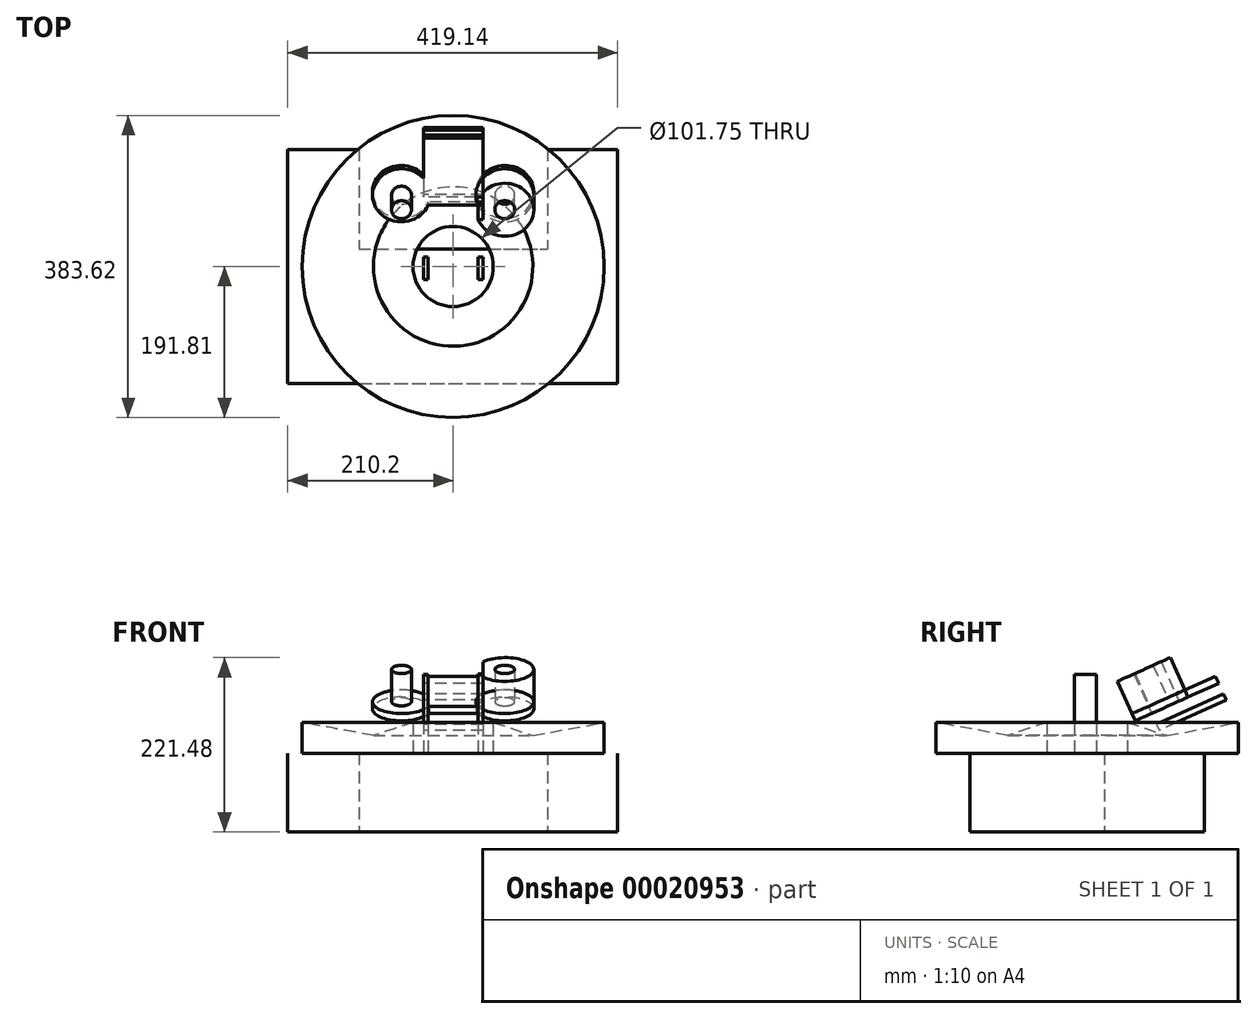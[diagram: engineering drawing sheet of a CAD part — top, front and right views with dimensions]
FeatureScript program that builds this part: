
annotation { "Feature Type Name" : "Feature", "Feature Type Description" : "" }
export const myFeature = defineFeature(function(context is Context, id is Id, definition is map)
    precondition{}
    {
        {
            var Q0;
            Q0=qCreatedBy(makeId("Top.planeOp"),FACE);
            var sketch = newSketch(context, id + "F0", { "sketchPlane" : qUnion([Q0])});
            skLineSegment(sketch, "E0.bottom", {"start": v(-210.2, 148.75) * mm, "end": v(208.94, 148.75) * mm});
            skLineSegment(sketch, "E0.top", {"start": v(-210.2, -148.75) * mm, "end": v(208.94, -148.75) * mm});
            skLineSegment(sketch, "E0.left", {"start": v(-210.2, 148.75) * mm, "end": v(-210.2, -148.75) * mm});
            skLineSegment(sketch, "E0.right", {"start": v(208.94, 148.75) * mm, "end": v(208.94, -148.75) * mm});
            skLineSegment(sketch, "E1", {"start": v(-0.63, 148.75) * mm, "end": v(0, 0) * mm, "construction": true});
            skLineSegment(sketch, "E2", {"start": v(0, 0) * mm, "end": v(0, -148.75) * mm, "construction": true});
            skLineSegment(sketch, "E3", {"start": v(0, 0) * mm, "end": v(-210.2, -0.9) * mm, "construction": true});
            skLineSegment(sketch, "E4", {"start": v(-210.2, -0.9) * mm, "end": v(0, 0) * mm, "construction": true});
            skLineSegment(sketch, "E5", {"start": v(0, 0) * mm, "end": v(208.94, 0.89) * mm, "construction": true});
            skLineSegment(sketch, "E6.bottom", {"start": v(-119.71, 148.75) * mm, "end": v(119.71, 148.75) * mm});
            skLineSegment(sketch, "E6.top", {"start": v(-119.71, 21.99) * mm, "end": v(119.71, 21.99) * mm});
            skLineSegment(sketch, "E6.left", {"start": v(-119.71, 148.75) * mm, "end": v(-119.71, 21.99) * mm});
            skLineSegment(sketch, "E6.right", {"start": v(119.71, 148.75) * mm, "end": v(119.71, 21.99) * mm});
            skPoint(sketch, "E7", {"position": v(0, 21.99) * mm});
            skSolve(sketch);
        }
        {
            var Q0;
            Q0=makeQuery(id+"F0.imprint","IMPRINT",FACE,{"disambiguationData":[TD([[makeQuery(id+"F0.imprint","IMPRINT",EDGE,{"derivedFrom":sQuery(id+"F0.wireOp",EDGE,"E0.top")}),1.0]])]});
            extrude(context, id + "F1", {"entities" : qUnion([Q0]), "depth" : 100 * mm});
        }
        {
            var Q0;
            Q0=makeQuery(id+"F1.opExtrude","CAP_FACE",FACE,{"disambiguationData":[OSD([sQuery(id+"F0.wireOp",EDGE,"E0.bottom"),sQuery(id+"F0.wireOp",EDGE,"E0.top"),sQuery(id+"F0.wireOp",EDGE,"E0.left"),sQuery(id+"F0.wireOp",EDGE,"E0.right"),sQuery(id+"F0.wireOp",EDGE,"E6.top"),sQuery(id+"F0.wireOp",EDGE,"E6.left"),sQuery(id+"F0.wireOp",EDGE,"E6.right")])],"isStart":false});
            var sketch = newSketch(context, id + "F2", { "sketchPlane" : qUnion([Q0])});
            skCircle(sketch, "E8", {"center": v(0, 0) * mm, "radius": 191.8 * mm});
            skCircle(sketch, "E9", {"center": v(0, 0) * mm, "radius": 50.88 * mm});
            skLineSegment(sketch, "E10.bottom", {"start": v(-37.83, 11.78) * mm, "end": v(-31.7, 11.78) * mm});
            skLineSegment(sketch, "E10.top", {"start": v(-37.83, -16.3) * mm, "end": v(-31.7, -16.3) * mm});
            skLineSegment(sketch, "E10.left", {"start": v(-37.83, 11.78) * mm, "end": v(-37.83, -16.3) * mm});
            skLineSegment(sketch, "E10.right", {"start": v(-31.7, 11.78) * mm, "end": v(-31.7, -16.3) * mm});
            skLineSegment(sketch, "E11", {"start": v(0, 0) * mm, "end": v(0, -33.08) * mm, "construction": true});
            skPoint(sketch, "E11.endSnap0", {"position": v(0, 21.99) * mm});
            skLineSegment(sketch, "E12.MirrorCS", {"start": v(37.83, 11.78) * mm, "end": v(37.83, -16.3) * mm});
            skLineSegment(sketch, "E13.MirrorCS", {"start": v(37.83, -16.3) * mm, "end": v(31.7, -16.3) * mm});
            skLineSegment(sketch, "E14.MirrorCS", {"start": v(31.7, 11.78) * mm, "end": v(31.7, -16.3) * mm});
            skLineSegment(sketch, "E15.MirrorCS", {"start": v(37.83, 11.78) * mm, "end": v(31.7, 11.78) * mm});
            skSolve(sketch);
        }
        {
            var Q0;
            Q0=qCreatedBy(makeId("Front.planeOp"),FACE);
            var sketch = newSketch(context, id + "F3", { "sketchPlane" : qUnion([Q0])});
            skLineSegment(sketch, "E16.0", {"start": v(-50.88, 100) * mm, "end": v(50.88, 100) * mm, "construction": true});
            skLineSegment(sketch, "E17.0", {"start": v(-191.8, 100) * mm, "end": v(191.8, 100) * mm, "construction": true});
            skLineSegment(sketch, "E18.bottom", {"start": v(50.88, 100) * mm, "end": v(191.8, 100) * mm});
            skLineSegment(sketch, "E18.left", {"start": v(50.88, 100) * mm, "end": v(50.88, 139.11) * mm});
            skLineSegment(sketch, "E18.right", {"start": v(191.8, 100) * mm, "end": v(191.8, 139.11) * mm});
            skLineSegment(sketch, "E19", {"start": v(50.88, 139.11) * mm, "end": v(101.24, 122.54) * mm});
            skLineSegment(sketch, "E20", {"start": v(191.8, 139.11) * mm, "end": v(101.24, 122.54) * mm});
            skLineSegment(sketch, "E21", {"start": v(0, 100) * mm, "end": v(0, 133.45) * mm, "construction": true});
            skPoint(sketch, "E21.endSnap0", {"position": v(0, 100) * mm});
            skSolve(sketch);
        }
        {
            var Q0;
            Q0=makeQuery(id+"F3.imprint","IMPRINT",FACE,{"disambiguationData":[TD([[makeQuery(id+"F3.imprint","IMPRINT",EDGE,{"derivedFrom":sQuery(id+"F3.wireOp",EDGE,"E18.bottom")}),1.0]])]});
            var Q1;
            Q1=sQuery(id+"F3.wireOp",EDGE,"E21");
            revolve(context, id + "F4", {"entities" : qUnion([Q0]), "axis" : qUnion([Q1]), "revolveType" : RevolveType.FULL});
        }
        {
            var Q0;
            Q0=makeQuery(id+"F2.imprint","IMPRINT",FACE,{"disambiguationData":[TD([[makeQuery(id+"F2.imprint","IMPRINT",EDGE,{"derivedFrom":sQuery(id+"F2.wireOp",EDGE,"E10.bottom")}),-1.0]])]});
            var Q1;
            Q1=makeQuery(id+"F2.imprint","IMPRINT",FACE,{"disambiguationData":[TD([[makeQuery(id+"F2.imprint","IMPRINT",EDGE,{"derivedFrom":sQuery(id+"F2.wireOp",EDGE,"E12.MirrorCS")}),-1.0]])]});
            extrude(context, id + "F5", {"entities" : qUnion([Q0, Q1]), "operationType" : NewBodyOperationType.ADD, "depth" : 100 * mm});
        }
        {
            var Q0;
            Q0=makeQuery(id+"F1.opExtrude","SWEPT_FACE",FACE,{"disambiguationData":[OSD([sQuery(id+"F0.wireOp",EDGE,"E0.left")])]});
            var sketch = newSketch(context, id + "F6", { "sketchPlane" : qUnion([Q0])});
            skLineSegment(sketch, "E22", {"start": v(-176.77, 167.45) * mm, "end": v(-91.54, 129.23) * mm});
            skLineSegment(sketch, "E23", {"start": v(-176.77, 167.45) * mm, "end": v(-173.35, 175.07) * mm});
            skLineSegment(sketch, "E24", {"start": v(-173.35, 175.07) * mm, "end": v(-88.12, 136.85) * mm});
            skLineSegment(sketch, "E25", {"start": v(-88.12, 136.85) * mm, "end": v(-91.54, 129.23) * mm});
            skSolve(sketch);
        }
        {
            var Q0;
            Q0=makeQuery(id+"F6.imprint","IMPRINT",FACE,{"disambiguationData":[TD([[makeQuery(id+"F6.imprint","IMPRINT",EDGE,{"derivedFrom":sQuery(id+"F6.wireOp",EDGE,"E22")}),1.0]])]});
            var Q1;
            Q1=makeQuery(id+"F5.opExtrude","SWEPT_FACE",FACE,{"disambiguationData":[OSD([sQuery(id+"F2.wireOp",EDGE,"E12.MirrorCS")])]});
            var Q2;
            Q2=makeQuery(id+"F5.opExtrude","SWEPT_FACE",FACE,{"disambiguationData":[OSD([sQuery(id+"F2.wireOp",EDGE,"E10.left")])]});
            extrude(context, id + "F7", {"entities" : qUnion([Q0]), "endBound" : BoundingType.UP_TO_SURFACE, "oppositeDirection" : true, "endBoundEntityFace" : qUnion([Q1]), "depth" : 25 * mm, "hasSecondDirection" : true, "secondDirectionBound" : SecondDirectionBoundingType.UP_TO_SURFACE, "secondDirectionOppositeDirection" : true, "secondDirectionBoundEntityFace" : qUnion([Q2]), "secondDirectionDepth" : 25 * mm});
        }
        {
            var Q0;
            Q0=makeQuery(id+"F7.opExtrude","SWEPT_FACE",FACE,{"disambiguationData":[OSD([sQuery(id+"F6.wireOp",EDGE,"E24")])]});
            var sketch = newSketch(context, id + "F8", { "sketchPlane" : qUnion([Q0])});
            skPoint(sketch, "E26.0", {"position": v(0, 136.4) * mm});
            skPoint(sketch, "E27.0", {"position": v(0, 229.81) * mm});
            skLineSegment(sketch, "E28", {"start": v(0, 229.81) * mm, "end": v(0, 136.4) * mm, "construction": true});
            skCircle(sketch, "E29", {"center": v(-65.61, 150.32) * mm, "radius": 36.81 * mm});
            skCircle(sketch, "E30", {"center": v(-65.61, 150.32) * mm, "radius": 12.58 * mm});
            skCircle(sketch, "E31.MirrorC", {"center": v(65.61, 150.32) * mm, "radius": 12.58 * mm});
            skCircle(sketch, "E32.MirrorC", {"center": v(65.61, 150.32) * mm, "radius": 36.81 * mm});
            skSolve(sketch);
        }
        {
            var Q0;
            Q0=makeQuery(id+"F8.imprint","IMPRINT",FACE,{"disambiguationData":[TD([[makeQuery(id+"F8.imprint","IMPRINT",EDGE,{"derivedFrom":sQuery(id+"F8.wireOp",EDGE,"E30")}),-1.0]])]});
            var Q1;
            Q1=makeQuery(id+"F8.imprint","IMPRINT",FACE,{"disambiguationData":[TD([[makeQuery(id+"F8.imprint","IMPRINT",EDGE,{"derivedFrom":sQuery(id+"F8.wireOp",EDGE,"E31.MirrorC")}),1.0]])]});
            var Q2;
            {var subQ0=sQuery(id+"F8.wireOp",EDGE,"E29");var subQ1=makeQuery(id+"F6.imprint","IMPRINT",EDGE,{"derivedFrom":sQuery(id+"F6.wireOp",EDGE,"E24")});var subQ2=makeQuery(id+"F7.opExtrude","TWEAK_EDGE",EDGE,{"derivedFrom":[makeQuery(id+"F5.opExtrude","SWEPT_FACE",FACE,{"disambiguationData":[OSD([sQuery(id+"F2.wireOp",EDGE,"E10.left")])]}),subQ1]});var subQ3=makeQuery(id+"F8.imprint","INTERSECT",VERTEX,{"derivedFrom":[subQ2,subQ0]});Q2=makeQuery(id+"F8.imprint","IMPRINT",FACE,{"disambiguationData":[TD([[makeQuery(id+"F8.imprint","IMPRINT",EDGE,{"disambiguationData":[TD([[subQ3,1.0]])],"derivedFrom":subQ0}),1.0]])]});}
            var Q3;
            {var subQ0=sQuery(id+"F8.wireOp",EDGE,"E32.MirrorC");var subQ1=makeQuery(id+"F6.imprint","IMPRINT",EDGE,{"derivedFrom":sQuery(id+"F6.wireOp",EDGE,"E24")});var subQ2=makeQuery(id+"F7.opExtrude","TWEAK_EDGE",EDGE,{"derivedFrom":[makeQuery(id+"F5.opExtrude","SWEPT_FACE",FACE,{"disambiguationData":[OSD([sQuery(id+"F2.wireOp",EDGE,"E12.MirrorCS")])]}),subQ1]});var subQ3=makeQuery(id+"F8.imprint","INTERSECT",VERTEX,{"derivedFrom":[subQ2,subQ0]});Q3=makeQuery(id+"F8.imprint","IMPRINT",FACE,{"disambiguationData":[TD([[makeQuery(id+"F8.imprint","IMPRINT",EDGE,{"disambiguationData":[TD([[subQ3,1.0]])],"derivedFrom":subQ0}),-1.0]])]});}
            var Q4;
            Q4=makeQuery(id+"F8.imprint","IMPRINT",FACE,{"disambiguationData":[TD([[makeQuery(id+"F8.imprint","IMPRINT",EDGE,{"derivedFrom":sQuery(id+"F8.wireOp",EDGE,"E30")}),1.0]])]});
            var Q5;
            Q5=makeQuery(id+"F8.imprint","IMPRINT",FACE,{"disambiguationData":[TD([[makeQuery(id+"F8.imprint","IMPRINT",EDGE,{"derivedFrom":sQuery(id+"F8.wireOp",EDGE,"E31.MirrorC")}),-1.0]])]});
            extrude(context, id + "F9", {"entities" : qUnion([Q0, Q1, Q2, Q3, Q4, Q5]), "depth" : 25 * mm, "hasSecondDirection" : true, "secondDirectionOppositeDirection" : false, "secondDirectionDepth" : 15 * mm});
        }
        {
            var Q0;
            Q0=makeQuery(id+"F8.imprint","IMPRINT",FACE,{"disambiguationData":[TD([[makeQuery(id+"F8.imprint","IMPRINT",EDGE,{"derivedFrom":sQuery(id+"F8.wireOp",EDGE,"E30")}),1.0]])]});
            var Q1;
            Q1=makeQuery(id+"F8.imprint","IMPRINT",FACE,{"disambiguationData":[TD([[makeQuery(id+"F8.imprint","IMPRINT",EDGE,{"derivedFrom":sQuery(id+"F8.wireOp",EDGE,"E31.MirrorC")}),-1.0]])]});
            var Q2;
            Q2=makeQuery(id+"F9.opExtrude","CAP_FACE",FACE,{"disambiguationData":[OSD([sQuery(id+"F8.wireOp",EDGE,"E29")])],"isStart":false});
            extrude(context, id + "F10", {"entities" : qUnion([Q0, Q1]), "depth" : 70 * mm, "hasSecondDirection" : true, "secondDirectionBound" : SecondDirectionBoundingType.UP_TO_SURFACE, "secondDirectionOppositeDirection" : false, "secondDirectionBoundEntityFace" : qUnion([Q2]), "secondDirectionDepth" : 25 * mm});
        }
    });
